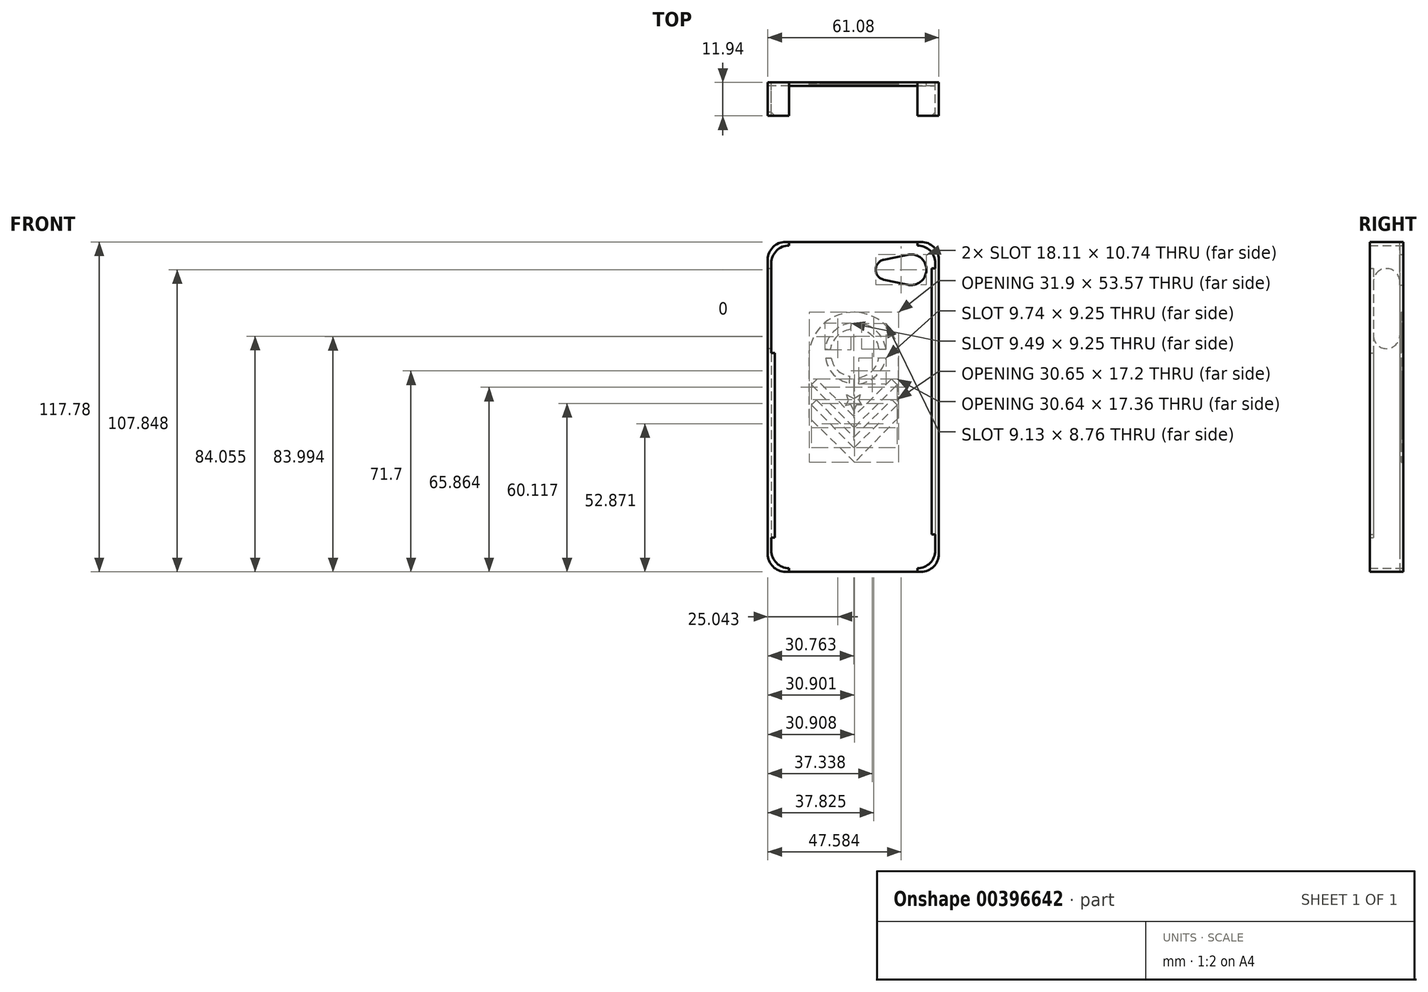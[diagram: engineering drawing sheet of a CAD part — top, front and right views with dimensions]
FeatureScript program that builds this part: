
annotation { "Feature Type Name" : "Feature", "Feature Type Description" : "" }
export const myFeature = defineFeature(function(context is Context, id is Id, definition is map)
    precondition{}
    {
        {
            var Q0;
            Q0=qCreatedBy(makeId("Front.planeOp"),FACE);
            var sketch = newSketch(context, id + "F0", { "sketchPlane" : qUnion([Q0])});
            skLineSegment(sketch, "E0.left", {"start": v(-75.12, 56.4) * mm, "end": v(-75.12, -46.14) * mm});
            skLineSegment(sketch, "E0.right", {"start": v(-16.58, 56.4) * mm, "end": v(-16.58, -46.14) * mm});
            skPoint(sketch, "E1.visualSharp", {"position": v(-16.58, 62.75) * mm});
            skArc(sketch, "E1.filletArc", {"start": v(-16.58, 56.4) * mm, "mid": v(-18.43, 60.88) * mm, "end": v(-22.9, 62.75) * mm});
            skPoint(sketch, "E2.visualSharp", {"position": v(-75.12, 62.75) * mm});
            skArc(sketch, "E2.filletArc", {"start": v(-68.77, 62.75) * mm, "mid": v(-73.26, 60.89) * mm, "end": v(-75.12, 56.4) * mm});
            skPoint(sketch, "E3.visualSharp", {"position": v(-75.12, -52.5) * mm});
            skArc(sketch, "E3.filletArc", {"start": v(-75.12, -46.14) * mm, "mid": v(-73.26, -50.63) * mm, "end": v(-68.77, -52.5) * mm});
            skPoint(sketch, "E4.visualSharp", {"position": v(-16.58, -52.5) * mm});
            skArc(sketch, "E4.filletArc", {"start": v(-22.93, -52.5) * mm, "mid": v(-18.44, -50.63) * mm, "end": v(-16.58, -46.14) * mm});
            skLineSegment(sketch, "E5.bottom", {"start": v(-70.04, 64.02) * mm, "end": v(-68.77, 64.02) * mm});
            skLineSegment(sketch, "E5.top", {"start": v(-70.04, -53.76) * mm, "end": v(-68.77, -53.76) * mm});
            skLineSegment(sketch, "E5.left", {"start": v(-76.4, 57.67) * mm, "end": v(-76.4, -47.41) * mm});
            skLineSegment(sketch, "E5.right", {"start": v(-15.3, 57.67) * mm, "end": v(-15.3, -47.41) * mm});
            skPoint(sketch, "E6.visualSharp", {"position": v(-15.3, 64.02) * mm});
            skArc(sketch, "E6.filletArc", {"start": v(-15.3, 57.67) * mm, "mid": v(-17.17, 62.16) * mm, "end": v(-21.66, 64.02) * mm});
            skPoint(sketch, "E7.visualSharp", {"position": v(-76.4, 64.02) * mm});
            skArc(sketch, "E7.filletArc", {"start": v(-70.04, 64.02) * mm, "mid": v(-74.53, 62.16) * mm, "end": v(-76.4, 57.67) * mm});
            skPoint(sketch, "E8.visualSharp", {"position": v(-76.4, -53.76) * mm});
            skArc(sketch, "E8.filletArc", {"start": v(-76.4, -47.41) * mm, "mid": v(-74.53, -51.9) * mm, "end": v(-70.04, -53.76) * mm});
            skPoint(sketch, "E9.visualSharp", {"position": v(-15.3, -53.76) * mm});
            skArc(sketch, "E9.filletArc", {"start": v(-21.66, -53.76) * mm, "mid": v(-17.17, -51.9) * mm, "end": v(-15.3, -47.41) * mm});
            skLineSegment(sketch, "E10", {"start": v(-68.77, -52.5) * mm, "end": v(-68.77, -53.76) * mm});
            skLineSegment(sketch, "E11", {"start": v(-22.93, -52.5) * mm, "end": v(-22.93, -53.76) * mm});
            skLineSegment(sketch, "E12.trimOffspring", {"start": v(-22.93, -53.76) * mm, "end": v(-21.66, -53.76) * mm});
            skLineSegment(sketch, "E13", {"start": v(-68.77, 62.75) * mm, "end": v(-68.77, 64.02) * mm});
            skLineSegment(sketch, "E14", {"start": v(-22.9, 62.75) * mm, "end": v(-22.9, 64.02) * mm});
            skLineSegment(sketch, "E15.trimOffspring", {"start": v(-22.9, 64.02) * mm, "end": v(-21.66, 64.02) * mm});
            skLineSegment(sketch, "E16", {"start": v(-68.77, 64.02) * mm, "end": v(-22.9, 64.02) * mm});
            skLineSegment(sketch, "E17", {"start": v(-68.77, -53.76) * mm, "end": v(-22.93, -53.76) * mm});
            skCircle(sketch, "E18", {"center": v(-25.24, 54.09) * mm, "radius": 5.48 * mm});
            skCircle(sketch, "E19", {"center": v(-34.23, 54.09) * mm, "radius": 3.64 * mm});
            skLineSegment(sketch, "E20", {"start": v(-26.36, 59.46) * mm, "end": v(-34.97, 57.65) * mm});
            skLineSegment(sketch, "E21", {"start": v(-26.36, 48.72) * mm, "end": v(-34.97, 50.53) * mm});
            skSolve(sketch);
        }
        {
            var Q0;
            Q0=makeQuery(id+"F0.imprint","IMPRINT",FACE,{"disambiguationData":[TD([[makeQuery(id+"F0.imprint","IMPRINT",EDGE,{"derivedFrom":sQuery(id+"F0.wireOp",EDGE,"E0.left")}),1.0]])]});
            extrude(context, id + "F1", {"entities" : qUnion([Q0]), "depth" : 1.27 * mm});
        }
        {
            var Q0;
            Q0=makeQuery(id+"F0.imprint","IMPRINT",FACE,{"disambiguationData":[TD([[makeQuery(id+"F0.imprint","IMPRINT",EDGE,{"derivedFrom":sQuery(id+"F0.wireOp",EDGE,"E0.left")}),-1.0]])]});
            var Q1;
            Q1=makeQuery(id+"F0.imprint","IMPRINT",FACE,{"disambiguationData":[TD([[makeQuery(id+"F0.imprint","IMPRINT",EDGE,{"derivedFrom":sQuery(id+"F0.wireOp",EDGE,"E0.right")}),1.0]])]});
            extrude(context, id + "F2", {"entities" : qUnion([Q0, Q1]), "operationType" : NewBodyOperationType.ADD, "depth" : 11.94 * mm});
        }
        {
            var Q0;
            Q0=makeQuery(id+"F2.opExtrude","SWEPT_FACE",FACE,{"disambiguationData":[OSD([sQuery(id+"F0.wireOp",EDGE,"E5.left")])]});
            var sketch = newSketch(context, id + "F3", { "sketchPlane" : qUnion([Q0])});
            skCircle(sketch, "E22", {"center": v(5.97, 49.8) * mm, "radius": 4.7 * mm});
            skCircle(sketch, "E23", {"center": v(5.97, 30.62) * mm, "radius": 4.7 * mm});
            skLineSegment(sketch, "E24", {"start": v(1.27, 49.8) * mm, "end": v(1.27, 30.62) * mm});
            skLineSegment(sketch, "E25", {"start": v(10.67, 30.62) * mm, "end": v(10.67, 49.8) * mm});
            skSolve(sketch);
        }
        {
            var Q0;
            {var subQ0=sQuery(id+"F3.wireOp",EDGE,"E24");Q0=makeQuery(id+"F3.imprint","IMPRINT",FACE,{"disambiguationData":[TD([[makeQuery(id+"F3.imprint","IMPRINT",EDGE,{"derivedFrom":subQ0}),1.0]])]});}
            var Q1;
            {var subQ0=sQuery(id+"F3.wireOp",EDGE,"E22");var subQ1=makeQuery(id+"F3.imprint","INTERSECT",VERTEX,{"derivedFrom":[subQ0,sQuery(id+"F3.wireOp",EDGE,"E24")]});Q1=makeQuery(id+"F3.imprint","IMPRINT",FACE,{"disambiguationData":[TD([[makeQuery(id+"F3.imprint","IMPRINT",EDGE,{"disambiguationData":[TD([[subQ1,1.0]])],"derivedFrom":subQ0}),1.0]])]});}
            var Q2;
            {var subQ0=sQuery(id+"F3.wireOp",EDGE,"E23");var subQ1=makeQuery(id+"F3.imprint","INTERSECT",VERTEX,{"derivedFrom":[subQ0,sQuery(id+"F3.wireOp",EDGE,"E24")]});Q2=makeQuery(id+"F3.imprint","IMPRINT",FACE,{"disambiguationData":[TD([[makeQuery(id+"F3.imprint","IMPRINT",EDGE,{"disambiguationData":[TD([[subQ1,1.0]])],"derivedFrom":subQ0}),1.0]])]});}
            extrude(context, id + "F4", {"entities" : qUnion([Q0, Q1, Q2]), "operationType" : NewBodyOperationType.REMOVE, "oppositeDirection" : true, "depth" : 25.4 * mm});
        }
        {
            var Q0;
            Q0=makeQuery(id+"F0.imprint","IMPRINT",FACE,{"disambiguationData":[TD([[makeQuery(id+"F0.imprint","IMPRINT",EDGE,{"derivedFrom":sQuery(id+"F0.wireOp",EDGE,"E0.right")}),-1.0]])]});
            extrude(context, id + "F5", {"entities" : qUnion([Q0]), "depth" : 1.27 * mm});
        }
        {
            var Q0;
            Q0=makeQuery(id+"F2.opExtrude","SWEPT_FACE",FACE,{"disambiguationData":[OSD([sQuery(id+"F0.wireOp",EDGE,"E0.left")])]});
            var sketch = newSketch(context, id + "F6", { "sketchPlane" : qUnion([Q0])});
            skLineSegment(sketch, "E26.bottom", {"start": v(-11.94, 24.38) * mm, "end": v(-10.67, 24.38) * mm});
            skLineSegment(sketch, "E26.top", {"start": v(-11.94, -41.62) * mm, "end": v(-10.67, -41.62) * mm});
            skLineSegment(sketch, "E26.left", {"start": v(-11.94, 24.38) * mm, "end": v(-11.94, -41.62) * mm});
            skLineSegment(sketch, "E26.right", {"start": v(-10.67, 24.38) * mm, "end": v(-10.67, -41.62) * mm});
            skSolve(sketch);
        }
        {
            var Q0;
            Q0=makeQuery(id+"F6.imprint","IMPRINT",FACE,{"disambiguationData":[TD([[makeQuery(id+"F6.imprint","IMPRINT",EDGE,{"derivedFrom":sQuery(id+"F6.wireOp",EDGE,"E26.bottom")}),-1.0]])]});
            extrude(context, id + "F7", {"entities" : qUnion([Q0]), "operationType" : NewBodyOperationType.ADD, "depth" : 1.27 * mm});
        }
        {
            var Q0;
            Q0=makeQuery(id+"F2.opExtrude","SWEPT_FACE",FACE,{"disambiguationData":[OSD([sQuery(id+"F0.wireOp",EDGE,"E0.right")])]});
            var sketch = newSketch(context, id + "F8", { "sketchPlane" : qUnion([Q0])});
            skLineSegment(sketch, "E27.bottom", {"start": v(11.94, 54.52) * mm, "end": v(10.67, 54.52) * mm});
            skLineSegment(sketch, "E27.top", {"start": v(11.94, -40.48) * mm, "end": v(10.67, -40.48) * mm});
            skLineSegment(sketch, "E27.left", {"start": v(11.94, 54.52) * mm, "end": v(11.94, -40.48) * mm});
            skLineSegment(sketch, "E27.right", {"start": v(10.67, 54.52) * mm, "end": v(10.67, -40.48) * mm});
            skSolve(sketch);
        }
        {
            var Q0;
            Q0=makeQuery(id+"F8.imprint","IMPRINT",FACE,{"disambiguationData":[TD([[makeQuery(id+"F8.imprint","IMPRINT",EDGE,{"derivedFrom":sQuery(id+"F8.wireOp",EDGE,"E27.bottom")}),1.0]])]});
            extrude(context, id + "F9", {"entities" : qUnion([Q0]), "operationType" : NewBodyOperationType.ADD, "depth" : 1.27 * mm});
        }
        {
            var Q0;
            Q0=makeQuery(id+"F9.opExtrude","SWEPT_FACE",FACE,{"disambiguationData":[OSD([sQuery(id+"F8.wireOp",EDGE,"E27.bottom")])]});
            var sketch = newSketch(context, id + "F10", { "sketchPlane" : qUnion([Q0])});
            skLineSegment(sketch, "E28", {"start": v(-16.58, -10.67) * mm, "end": v(-17.85, -11.94) * mm});
            skSolve(sketch);
        }
        {
            var Q0;
            Q0=makeQuery(id+"F10.imprint","IMPRINT",FACE,{"disambiguationData":[TD([[makeQuery(id+"F10.imprint","IMPRINT",EDGE,{"derivedFrom":sQuery(id+"F10.wireOp",EDGE,"E28")}),-1.0]])]});
            extrude(context, id + "F11", {"entities" : qUnion([Q0]), "operationType" : NewBodyOperationType.REMOVE, "oppositeDirection" : true, "depth" : 95 * mm});
        }
        {
            var Q0;
            Q0=makeQuery(id+"F7.opExtrude","SWEPT_FACE",FACE,{"disambiguationData":[OSD([sQuery(id+"F6.wireOp",EDGE,"E26.bottom")])]});
            var sketch = newSketch(context, id + "F12", { "sketchPlane" : qUnion([Q0])});
            skLineSegment(sketch, "E29", {"start": v(-75.12, -10.67) * mm, "end": v(-73.85, -11.94) * mm});
            skSolve(sketch);
        }
        {
            var Q0;
            Q0=makeQuery(id+"F12.imprint","IMPRINT",FACE,{"disambiguationData":[TD([[makeQuery(id+"F12.imprint","IMPRINT",EDGE,{"derivedFrom":sQuery(id+"F12.wireOp",EDGE,"E29")}),1.0]])]});
            extrude(context, id + "F13", {"entities" : qUnion([Q0]), "operationType" : NewBodyOperationType.REMOVE, "oppositeDirection" : true, "depth" : 68.58 * mm});
        }
        {
            var Q0;
            {var subQ0=sQuery(id+"F0.wireOp",EDGE,"E14");var subQ1=sQuery(id+"F0.wireOp",EDGE,"E11");var subQ2=sQuery(id+"F0.wireOp",EDGE,"E4.filletArc");var subQ3=sQuery(id+"F0.wireOp",EDGE,"E1.filletArc");var subQ4=sQuery(id+"F0.wireOp",EDGE,"E0.right");var subQ5=sQuery(id+"F0.wireOp",EDGE,"E13");var subQ6=sQuery(id+"F0.wireOp",EDGE,"E10");var subQ7=sQuery(id+"F0.wireOp",EDGE,"E3.filletArc");var subQ8=sQuery(id+"F0.wireOp",EDGE,"E2.filletArc");var subQ9=sQuery(id+"F0.wireOp",EDGE,"E0.left");Q0=makeQuery(id+"F2.boolean.opBoolean","MERGE",FACE,{"derivedFrom":[makeQuery(id+"F1.opExtrude","CAP_FACE",FACE,{"disambiguationData":[OSD([subQ9,subQ4,subQ3,subQ8,subQ7,subQ2,subQ6,subQ1,subQ5,subQ0,sQuery(id+"F0.wireOp",EDGE,"E16"),sQuery(id+"F0.wireOp",EDGE,"E17"),sQuery(id+"F0.wireOp",EDGE,"E18"),sQuery(id+"F0.wireOp",EDGE,"E19"),sQuery(id+"F0.wireOp",EDGE,"E20"),sQuery(id+"F0.wireOp",EDGE,"E21")])],"isStart":true}),makeQuery(id+"F2.opExtrude","CAP_FACE",FACE,{"disambiguationData":[OSD([subQ9,subQ8,subQ7,sQuery(id+"F0.wireOp",EDGE,"E5.bottom"),sQuery(id+"F0.wireOp",EDGE,"E5.top"),sQuery(id+"F0.wireOp",EDGE,"E5.left"),sQuery(id+"F0.wireOp",EDGE,"E7.filletArc"),sQuery(id+"F0.wireOp",EDGE,"E8.filletArc"),subQ6,subQ5])],"isStart":true}),makeQuery(id+"F2.opExtrude","CAP_FACE",FACE,{"disambiguationData":[OSD([subQ4,subQ3,subQ2,sQuery(id+"F0.wireOp",EDGE,"E5.right"),sQuery(id+"F0.wireOp",EDGE,"E6.filletArc"),sQuery(id+"F0.wireOp",EDGE,"E9.filletArc"),subQ1,sQuery(id+"F0.wireOp",EDGE,"E12.trimOffspring"),subQ0,sQuery(id+"F0.wireOp",EDGE,"E15.trimOffspring")])],"isStart":true})]});}
            var sketch = newSketch(context, id + "F14", { "sketchPlane" : qUnion([Q0])});
            skLineSegment(sketch, "E30", {"start": v(29.68, 1.26) * mm, "end": v(29.68, 24.76) * mm});
            skLineSegment(sketch, "E31", {"start": v(29.68, 1.26) * mm, "end": v(45.38, -14.68) * mm});
            skLineSegment(sketch, "E32", {"start": v(45.38, -14.68) * mm, "end": v(61.58, 1.26) * mm});
            skLineSegment(sketch, "E33", {"start": v(61.58, 1.26) * mm, "end": v(61.58, 25.24) * mm});
            skArc(sketch, "E34", {"start": v(61.58, 25.24) * mm, "mid": v(45.42, 38.9) * mm, "end": v(29.68, 24.76) * mm});
            skArc(sketch, "E35", {"start": v(36.74, 22.44) * mm, "mid": v(39.13, 17.93) * mm, "end": v(43.68, 15.63) * mm});
            skArc(sketch, "E36", {"start": v(34.18, 22.57) * mm, "mid": v(37.56, 16.37) * mm, "end": v(43.92, 13.31) * mm});
            skArc(sketch, "E37", {"start": v(42.95, 32.67) * mm, "mid": v(38.73, 30.16) * mm, "end": v(36.62, 25.73) * mm});
            skArc(sketch, "E38", {"start": v(42.95, 34.86) * mm, "mid": v(37.12, 31.68) * mm, "end": v(34.18, 25.73) * mm});
            skArc(sketch, "E39", {"start": v(55.97, 25.73) * mm, "mid": v(52.92, 31.93) * mm, "end": v(46.72, 34.98) * mm});
            skArc(sketch, "E40", {"start": v(54.15, 25.49) * mm, "mid": v(51.65, 30.3) * mm, "end": v(46.84, 32.8) * mm});
            skArc(sketch, "E41", {"start": v(47.09, 16.11) * mm, "mid": v(51.43, 18.18) * mm, "end": v(53.66, 22.44) * mm});
            skArc(sketch, "E42", {"start": v(47.2, 13.56) * mm, "mid": v(52.88, 16.65) * mm, "end": v(55.73, 22.44) * mm});
            skLineSegment(sketch, "E43", {"start": v(47.2, 13.56) * mm, "end": v(47.09, 16.11) * mm});
            skLineSegment(sketch, "E44", {"start": v(43.92, 13.31) * mm, "end": v(43.68, 15.63) * mm});
            skLineSegment(sketch, "E45", {"start": v(34.18, 22.57) * mm, "end": v(36.74, 22.44) * mm});
            skLineSegment(sketch, "E46", {"start": v(42.95, 34.86) * mm, "end": v(42.95, 32.67) * mm});
            skLineSegment(sketch, "E47", {"start": v(36.62, 25.73) * mm, "end": v(34.18, 25.73) * mm});
            skLineSegment(sketch, "E48", {"start": v(46.72, 34.98) * mm, "end": v(46.84, 32.8) * mm});
            skLineSegment(sketch, "E49", {"start": v(54.15, 25.49) * mm, "end": v(55.97, 25.73) * mm});
            skLineSegment(sketch, "E50", {"start": v(45.61, -2.32) * mm, "end": v(30.16, 13) * mm});
            skPoint(sketch, "E50.endSnap0", {"position": v(29.68, 13) * mm});
            skLineSegment(sketch, "E51", {"start": v(30.16, 13) * mm, "end": v(32.22, 15.04) * mm});
            skLineSegment(sketch, "E52", {"start": v(32.22, 15.04) * mm, "end": v(45.65, 1.72) * mm});
            skLineSegment(sketch, "E53", {"start": v(45.65, 1.72) * mm, "end": v(58.96, 14.83) * mm});
            skLineSegment(sketch, "E54", {"start": v(58.96, 14.83) * mm, "end": v(60.8, 13) * mm});
            skLineSegment(sketch, "E55", {"start": v(60.8, 13) * mm, "end": v(45.61, -2.32) * mm});
            skLineSegment(sketch, "E56", {"start": v(45.65, -9.49) * mm, "end": v(60.81, 5.82) * mm});
            skLineSegment(sketch, "E57", {"start": v(60.81, 5.82) * mm, "end": v(59.05, 7.57) * mm});
            skLineSegment(sketch, "E58", {"start": v(59.05, 7.57) * mm, "end": v(45.61, -5.66) * mm});
            skLineSegment(sketch, "E59", {"start": v(45.61, -5.66) * mm, "end": v(32.11, 7.7) * mm});
            skLineSegment(sketch, "E60", {"start": v(32.11, 7.7) * mm, "end": v(30.16, 5.74) * mm});
            skLineSegment(sketch, "E61", {"start": v(30.16, 5.74) * mm, "end": v(45.65, -9.49) * mm});
            skLineSegment(sketch, "E62", {"start": v(45.65, 3.73) * mm, "end": v(46.72, 5.99) * mm});
            skLineSegment(sketch, "E63", {"start": v(46.72, 5.99) * mm, "end": v(48.63, 5.53) * mm});
            skLineSegment(sketch, "E64", {"start": v(48.63, 5.53) * mm, "end": v(47.57, 7.3) * mm});
            skLineSegment(sketch, "E65", {"start": v(47.57, 7.3) * mm, "end": v(48.22, 9.44) * mm});
            skLineSegment(sketch, "E66", {"start": v(48.22, 9.44) * mm, "end": v(45.65, 8.1) * mm});
            skLineSegment(sketch, "E67", {"start": v(45.65, 8.1) * mm, "end": v(43.4, 9.52) * mm});
            skLineSegment(sketch, "E68", {"start": v(43.4, 9.52) * mm, "end": v(43.92, 7.58) * mm});
            skLineSegment(sketch, "E69", {"start": v(43.92, 7.58) * mm, "end": v(42.95, 5.82) * mm});
            skLineSegment(sketch, "E70", {"start": v(42.95, 5.82) * mm, "end": v(44.74, 5.82) * mm});
            skLineSegment(sketch, "E71", {"start": v(44.74, 5.82) * mm, "end": v(45.65, 3.73) * mm});
            skLineSegment(sketch, "E72", {"start": v(53.66, 22.44) * mm, "end": v(55.73, 22.44) * mm});
            skSolve(sketch);
        }
        {
            var Q0;
            Q0 = qSketchRegion(id + "F14", true);
            extrude(context, id + "F15", {"entities" : qUnion([Q0]), "operationType" : NewBodyOperationType.REMOVE, "oppositeDirection" : true, "depth" : 0.76 * mm});
        }
    });
